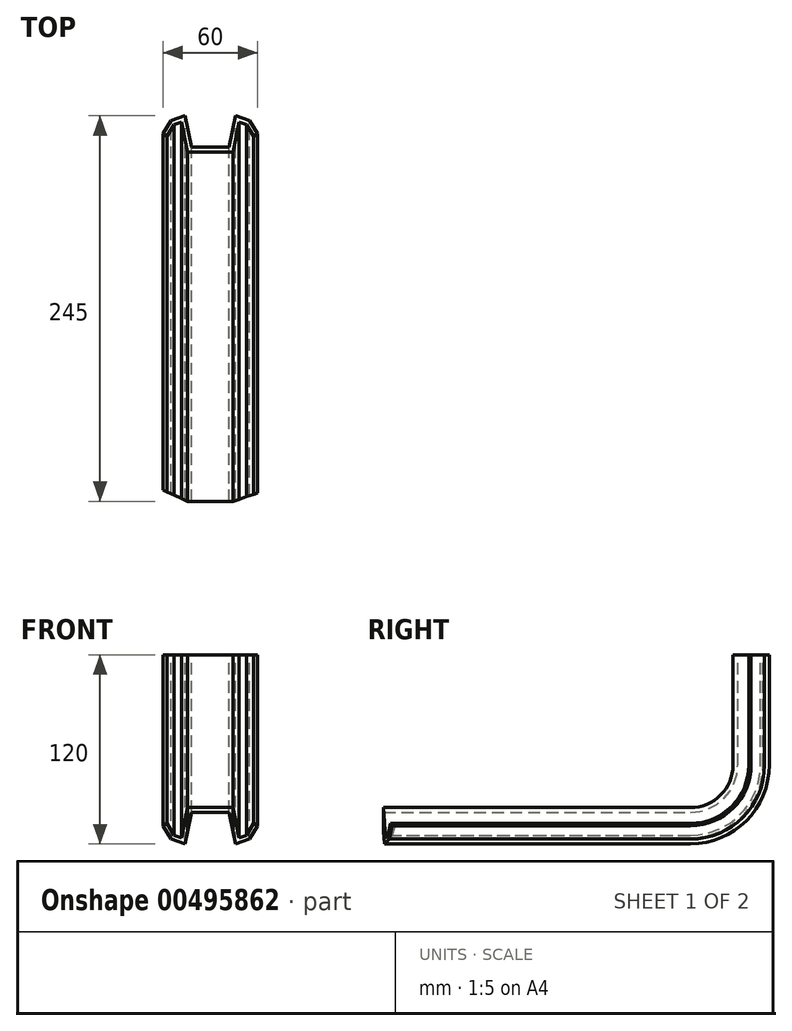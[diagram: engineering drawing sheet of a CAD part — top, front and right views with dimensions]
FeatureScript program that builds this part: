
annotation { "Feature Type Name" : "Feature", "Feature Type Description" : "" }
export const myFeature = defineFeature(function(context is Context, id is Id, definition is map)
    precondition{}
    {
        {
            var Q0;
            Q0=qCreatedBy(makeId("Front.planeOp"),FACE);
            var sketch = newSketch(context, id + "F0", { "sketchPlane" : qUnion([Q0])});
            skLineSegment(sketch, "E0", {"start": v(-30, 11.49) * mm, "end": v(-25.05, 3.02) * mm});
            skLineSegment(sketch, "E1", {"start": v(-25.05, 3.02) * mm, "end": v(-16, 0) * mm});
            skLineSegment(sketch, "E2", {"start": v(-16, 0) * mm, "end": v(-12, 20) * mm});
            skLineSegment(sketch, "E3", {"start": v(-12, 20) * mm, "end": v(0, 20) * mm});
            skLineSegment(sketch, "E4", {"start": v(0, 0) * mm, "end": v(0, 40.03) * mm, "construction": true});
            skLineSegment(sketch, "E5.0", {"start": v(-14.46, 23) * mm, "end": v(0, 23) * mm});
            skLineSegment(sketch, "E5.1", {"start": v(-18.27, 3.92) * mm, "end": v(-14.46, 23) * mm});
            skLineSegment(sketch, "E5.2", {"start": v(-23.03, 5.5) * mm, "end": v(-18.27, 3.92) * mm});
            skLineSegment(sketch, "E5.3", {"start": v(-27.41, 13) * mm, "end": v(-23.03, 5.5) * mm});
            skLineSegment(sketch, "E6", {"start": v(-30, 11.49) * mm, "end": v(-27.41, 13) * mm});
            skLineSegment(sketch, "E7.MirrorCS", {"start": v(14.46, 23) * mm, "end": v(0, 23) * mm});
            skLineSegment(sketch, "E8.MirrorCS", {"start": v(12, 20) * mm, "end": v(0, 20) * mm});
            skLineSegment(sketch, "E9.MirrorCS", {"start": v(18.27, 3.92) * mm, "end": v(14.46, 23) * mm});
            skLineSegment(sketch, "E10.MirrorCS", {"start": v(16, 0) * mm, "end": v(12, 20) * mm});
            skLineSegment(sketch, "E11.MirrorCS", {"start": v(25.05, 3.02) * mm, "end": v(16, 0) * mm});
            skLineSegment(sketch, "E12.MirrorCS", {"start": v(23.03, 5.5) * mm, "end": v(18.27, 3.92) * mm});
            skLineSegment(sketch, "E13.MirrorCS", {"start": v(27.41, 13) * mm, "end": v(23.03, 5.5) * mm});
            skLineSegment(sketch, "E14.MirrorCS", {"start": v(30, 11.49) * mm, "end": v(25.05, 3.02) * mm});
            skLineSegment(sketch, "E15.MirrorCS", {"start": v(30, 11.49) * mm, "end": v(27.41, 13) * mm});
            skSolve(sketch);
        }
        {
            var Q0;
            Q0=qCreatedBy(makeId("Right.planeOp"),FACE);
            var sketch = newSketch(context, id + "F1", { "sketchPlane" : qUnion([Q0])});
            skLineSegment(sketch, "E16", {"start": v(0, 0) * mm, "end": v(195, 0) * mm});
            skLineSegment(sketch, "E17", {"start": v(245, 50) * mm, "end": v(245, 120) * mm});
            skPoint(sketch, "E18.visualSharp", {"position": v(245, 0) * mm});
            skArc(sketch, "E18.filletArc", {"start": v(195, 0) * mm, "mid": v(230.36, 14.64) * mm, "end": v(245, 50) * mm});
            skSolve(sketch);
        }
        {
            var Q0;
            Q0=qSketchRegion(id+"F0",true);
            var Q1;
            Q1=qConstructionFilter(qBodyType(qCreatedBy(id+"F1",EDGE),BodyType.WIRE),ConstructionObject.NO);
            sweep(context, id + "F2", {"profiles" : qUnion([Q0]), "path" : qUnion([Q1])});
        }
        {
            var Q0;
            Q0=makeQuery(id+"F2.opSweep","SWEPT_FACE",FACE,{"disambiguationData":[OSD([sQuery(id+"F0.wireOp",EDGE,"E5.0"),sQuery(id+"F0.wireOp",EDGE,"E7.MirrorCS"),sQuery(id+"F1.wireOp",EDGE,"E16")])]});
            var sketch = newSketch(context, id + "F3", { "sketchPlane" : qUnion([Q0])});
            skLineSegment(sketch, "E19", {"start": v(-14.46, 0) * mm, "end": v(-33.17, 8.61) * mm});
            skLineSegment(sketch, "E20", {"start": v(-33.17, 8.61) * mm, "end": v(-33.17, -9.62) * mm});
            skLineSegment(sketch, "E21", {"start": v(-33.17, -9.62) * mm, "end": v(39.28, -9.62) * mm});
            skLineSegment(sketch, "E22", {"start": v(39.28, -9.62) * mm, "end": v(39.28, 8.61) * mm});
            skLineSegment(sketch, "E23", {"start": v(39.28, 8.61) * mm, "end": v(14.46, 0) * mm});
            skLineSegment(sketch, "E24", {"start": v(14.46, 0) * mm, "end": v(14.46, -4.23) * mm});
            skLineSegment(sketch, "E25", {"start": v(14.46, -4.23) * mm, "end": v(-14.46, -4.23) * mm});
            skLineSegment(sketch, "E26", {"start": v(-14.46, -4.23) * mm, "end": v(-14.46, 0) * mm});
            skSolve(sketch);
        }
        {
            var Q0;
            Q0=makeQuery(id+"F3.imprint","IMPRINT",FACE,{"disambiguationData":[TD([[makeQuery(id+"F3.imprint","IMPRINT",EDGE,{"derivedFrom":sQuery(id+"F3.wireOp",EDGE,"E19")}),1.0]])]});
            extrude(context, id + "F4", {"entities" : qUnion([Q0]), "operationType" : NewBodyOperationType.REMOVE, "oppositeDirection" : true, "depth" : 100 * mm});
        }
    });
